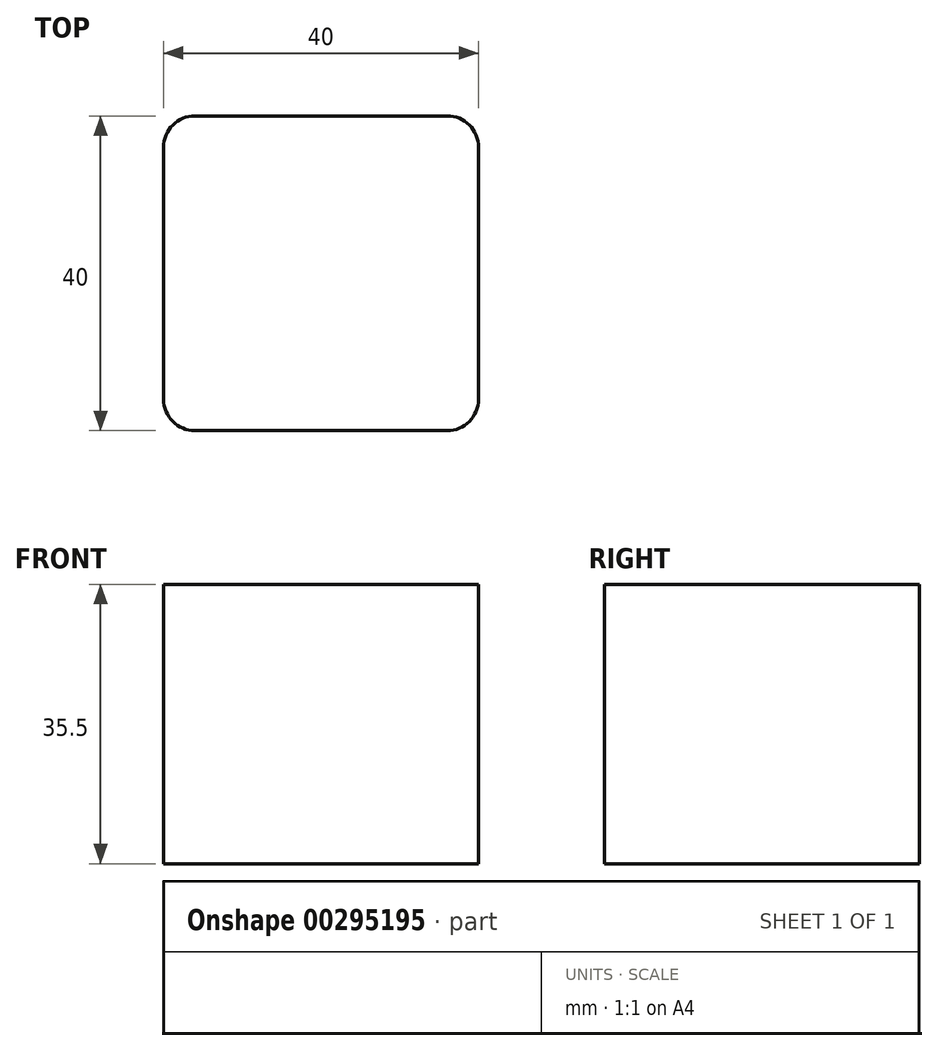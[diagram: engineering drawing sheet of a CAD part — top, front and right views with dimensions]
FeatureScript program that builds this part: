
annotation { "Feature Type Name" : "Feature", "Feature Type Description" : "" }
export const myFeature = defineFeature(function(context is Context, id is Id, definition is map)
    precondition{}
    {
        {
            var Q0;
            Q0=qCreatedBy(makeId("Top.planeOp"),FACE);
            var sketch = newSketch(context, id + "F0", { "sketchPlane" : qUnion([Q0])});
            skLineSegment(sketch, "E0.bottom", {"start": v(20, 20) * mm, "end": v(-20, 20) * mm});
            skLineSegment(sketch, "E0.top", {"start": v(20, -20) * mm, "end": v(-20, -20) * mm});
            skLineSegment(sketch, "E0.left", {"start": v(20, 20) * mm, "end": v(20, -20) * mm});
            skLineSegment(sketch, "E0.right", {"start": v(-20, 20) * mm, "end": v(-20, -20) * mm});
            skPoint(sketch, "E0.middle", {"position": v(0, 0) * mm});
            skSolve(sketch);
        }
        {
            var Q0;
            Q0=qSketchRegion(id+"F0",true);
            extrude(context, id + "F1", {"entities" : qUnion([Q0]), "depth" : 40 * mm});
        }
        {
            var Q0;
            Q0=makeQuery(id+"F1.opExtrude","CAP_FACE",FACE,{"disambiguationData":[OSD([sQuery(id+"F0.wireOp",EDGE,"E0.bottom"),sQuery(id+"F0.wireOp",EDGE,"E0.top"),sQuery(id+"F0.wireOp",EDGE,"E0.left"),sQuery(id+"F0.wireOp",EDGE,"E0.right")])],"isStart":false});
            var Q1;
            Q1=makeQuery(id+"F1.opExtrude","SWEPT_FACE",FACE,{"disambiguationData":[OSD([sQuery(id+"F0.wireOp",EDGE,"E0.left")])]});
            var Q2;
            Q2=makeQuery(id+"F1.opExtrude","SWEPT_FACE",FACE,{"disambiguationData":[OSD([sQuery(id+"F0.wireOp",EDGE,"E0.right")])]});
            var Q3;
            Q3=makeQuery(id+"F1.opExtrude","CAP_FACE",FACE,{"disambiguationData":[OSD([sQuery(id+"F0.wireOp",EDGE,"E0.bottom"),sQuery(id+"F0.wireOp",EDGE,"E0.top"),sQuery(id+"F0.wireOp",EDGE,"E0.left"),sQuery(id+"F0.wireOp",EDGE,"E0.right")])],"isStart":true});
            fillet(context, id + "F2", {"entities" : qUnion([Q0, Q1, Q2, Q3]), "radius" : 4 * mm, "tangentPropagation" : true, "allowEdgeOverflow" : false});
        }
        {
            var Q0;
            Q0=makeQuery(id+"F1.opExtrude","CAP_FACE",FACE,{"disambiguationData":[OSD([sQuery(id+"F0.wireOp",EDGE,"E0.bottom"),sQuery(id+"F0.wireOp",EDGE,"E0.top"),sQuery(id+"F0.wireOp",EDGE,"E0.left"),sQuery(id+"F0.wireOp",EDGE,"E0.right")])],"isStart":false});
            var sketch = newSketch(context, id + "F3", { "sketchPlane" : qUnion([Q0])});
            skLineSegment(sketch, "E1.bottom", {"start": v(43.58, -41.17) * mm, "end": v(-43.58, -41.17) * mm});
            skLineSegment(sketch, "E1.top", {"start": v(43.58, 41.17) * mm, "end": v(-43.58, 41.17) * mm});
            skLineSegment(sketch, "E1.left", {"start": v(43.58, -41.17) * mm, "end": v(43.58, 41.17) * mm});
            skLineSegment(sketch, "E1.right", {"start": v(-43.58, -41.17) * mm, "end": v(-43.58, 41.17) * mm});
            skPoint(sketch, "E1.middle", {"position": v(0, 0) * mm});
            skSolve(sketch);
        }
        {
            var Q0;
            Q0=qSketchRegion(id+"F3",true);
            extrude(context, id + "F4", {"entities" : qUnion([Q0]), "operationType" : NewBodyOperationType.REMOVE, "oppositeDirection" : true, "depth" : (2.5 + 40 - 24) * mm});
        }
        {
            var Q0;
            Q0=makeQuery(id+"F1.opExtrude","CAP_FACE",FACE,{"disambiguationData":[OSD([sQuery(id+"F0.wireOp",EDGE,"E0.bottom"),sQuery(id+"F0.wireOp",EDGE,"E0.top"),sQuery(id+"F0.wireOp",EDGE,"E0.left"),sQuery(id+"F0.wireOp",EDGE,"E0.right")])],"isStart":true});
            var sketch = newSketch(context, id + "F5", { "sketchPlane" : qUnion([Q0])});
            skLineSegment(sketch, "E2.bottom", {"start": v(-32.97, -34.84) * mm, "end": v(32.97, -34.84) * mm});
            skLineSegment(sketch, "E2.top", {"start": v(-32.97, 37.77) * mm, "end": v(32.97, 37.77) * mm});
            skLineSegment(sketch, "E2.left", {"start": v(-32.97, -34.84) * mm, "end": v(-32.97, 37.77) * mm});
            skLineSegment(sketch, "E2.right", {"start": v(32.97, -34.84) * mm, "end": v(32.97, 37.77) * mm});
            skPoint(sketch, "E2.middle", {"position": v(0, 1.46) * mm});
            skSolve(sketch);
        }
        {
            var Q0;
            Q0 = qSketchRegion(id + "F5", true);
            extrude(context, id + "F6", {"entities" : qUnion([Q0]), "operationType" : NewBodyOperationType.REMOVE, "oppositeDirection" : true, "depth" : 6.5 * mm});
        }
        {
            var Q0;
            Q0=makeQuery(id+"F4.boolean.opBoolean","COPY",FACE,{"derivedFrom":makeQuery(id+"F4.opExtrude","CAP_FACE",FACE,{"disambiguationData":[OSD([sQuery(id+"F3.wireOp",EDGE,"E1.bottom"),sQuery(id+"F3.wireOp",EDGE,"E1.top"),sQuery(id+"F3.wireOp",EDGE,"E1.left"),sQuery(id+"F3.wireOp",EDGE,"E1.right")])],"isStart":false})});
            extrude(context, id + "F7", {"entities" : qUnion([Q0]), "operationType" : NewBodyOperationType.ADD, "depth" : 20.5 * mm});
        }
        {
            var Q0;
            Q0=makeQuery(id+"F7.opExtrude","CAP_FACE",FACE,{"disambiguationData":[OSD([sQuery(id+"F3.wireOp",EDGE,"E1.bottom"),sQuery(id+"F3.wireOp",EDGE,"E1.top"),sQuery(id+"F3.wireOp",EDGE,"E1.left"),sQuery(id+"F3.wireOp",EDGE,"E1.right")])],"isStart":false});
            var sketch = newSketch(context, id + "F8", { "sketchPlane" : qUnion([Q0])});
            skLineSegment(sketch, "E3.bottom", {"start": v(-16.1, -21.1) * mm, "end": v(16.1, -21.1) * mm});
            skLineSegment(sketch, "E3.top", {"start": v(-16.1, 21.1) * mm, "end": v(16.1, 21.1) * mm});
            skLineSegment(sketch, "E3.left", {"start": v(-21.1, -16.1) * mm, "end": v(-21.1, 16.1) * mm});
            skLineSegment(sketch, "E3.right", {"start": v(21.1, -16.1) * mm, "end": v(21.1, 16.1) * mm});
            skPoint(sketch, "E3.middle", {"position": v(0, 0) * mm});
            skPoint(sketch, "E4.visualSharp", {"position": v(21.1, -21.1) * mm});
            skArc(sketch, "E4.filletArc", {"start": v(16.1, -21.1) * mm, "mid": v(19.64, -19.64) * mm, "end": v(21.1, -16.1) * mm});
            skPoint(sketch, "E5.visualSharp", {"position": v(-21.1, -21.1) * mm});
            skArc(sketch, "E5.filletArc", {"start": v(-21.1, -16.1) * mm, "mid": v(-19.64, -19.64) * mm, "end": v(-16.1, -21.1) * mm});
            skPoint(sketch, "E6.visualSharp", {"position": v(-21.1, 21.1) * mm});
            skArc(sketch, "E6.filletArc", {"start": v(-16.1, 21.1) * mm, "mid": v(-19.64, 19.64) * mm, "end": v(-21.1, 16.1) * mm});
            skPoint(sketch, "E7.visualSharp", {"position": v(21.1, 21.1) * mm});
            skArc(sketch, "E7.filletArc", {"start": v(21.1, 16.1) * mm, "mid": v(19.64, 19.64) * mm, "end": v(16.1, 21.1) * mm});
            skSolve(sketch);
        }
        {
            var Q0;
            Q0=makeQuery(id+"F8.imprint","IMPRINT",FACE,{"disambiguationData":[TD([[makeQuery(id+"F8.imprint","IMPRINT",EDGE,{"derivedFrom":sQuery(id+"F8.wireOp",EDGE,"E3.bottom")}),1.0]])]});
            extrude(context, id + "F9", {"entities" : qUnion([Q0]), "operationType" : NewBodyOperationType.REMOVE, "oppositeDirection" : true, "depth" : 4 * mm});
        }
    });
